# Revit family: Drinking_Fountain-Haws_Corporation-Pedestal_3500
name_source: partatom
category: Plumbing Fixtures
revit_build: Autodesk Revit Architecture 2015 (Build: 20140606_1530(x64)
units: mm (PartAtom-declared; Revit-internal decimal feet)

## types (3) — shared parameters
Assembly Code = D2010810
Bowl Height = 27"
Bowl Length = 18"
Components = Metal - Haws Corporation - High Polished Stainless Steel
Cost = $0.00
Cost Note = For Cost information please visit the Resource tab in the Product Page URL
Flow = 0.00 GPM
Keynote = 15410.A1
Manufacturer = Haws Corporation
Pedestal = Metal - Haws Corporation - Green Powder Coated Finish
Product Documentation Link = http://www.hawsco.com
Product Page URL = http://www.hawsco.com
Series = 3500 heavy-duty StreetSmart series
To Spot Outlet = 35 1/2"
URL = http://www.hawsco.com
Version = 2014-v2.0a
Water Way Note = 100% Lead Free Water Way

## per-type parameters (varying)
| type | CWFU | Description | HW Connection | HWFU | Model | Sanitary Radius | Supply Radius | Type Comments | Unit Length | Vent Connection | WFU | Waste Connection |
| 3500 | 1 | Green powder-coat paint finish is standard with nine other powder-coat colors available at no charge | No | 1 | 3500 | 1/2" | 0" | Provide for twice the users as regular drinking fountains | 30" | No | 1 | Yes |
| 3500FR | 2 | Use a freeze-resistant valve assembly to provide year round operation | No | 2 | 3500FR | 1" | 1/2" | Provide for twice the users as regular drinking fountains | 30" | No | 2 | Yes |
| 3500D | 3 | Green powder-coat paint finish is standard with nine other powder-coat colors available at no charge | Yes | 3 | 3380G | 1" | 1/2" | Ground level dog fountain allows for pet owners to easily supply their animal with a cool flowing stream of water | 38" | Yes | 3 | No |

## geometry (parser evidence)
native form markers: Blend x30, Sweep x5
no freeform markers — native parametric forms only
